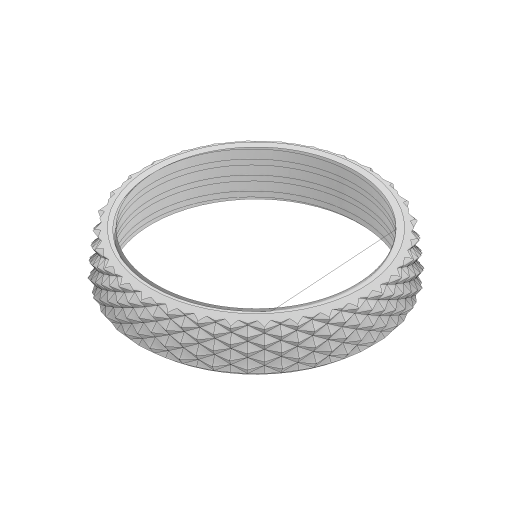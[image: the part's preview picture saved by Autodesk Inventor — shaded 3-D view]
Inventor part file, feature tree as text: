
AUTODESK INVENTOR PART (.ipt)
format: ipt  version: 2023 (Build 270158000, 158)  size: 4,238,336 bytes
history: native  units: mm
features: sketch x5, helix x3, draft x2, extrude x1, pattern_circular x1, mirror x1, revolve x1, projected_geometry x1
ambient origin geometry x8: Origin, YZ Plane, XZ Plane, XY Plane, X Axis, Y Axis, Z Axis, Center Point
bodies: Solid1 (feature_tree)
feature tree (15):
  extrude  "Extrusion1"  Depth=6.52mm TaperAngle=0.0deg
  draft  "FaceDraft1"
  sketch  "Sketch2"  dims[d7=2.0mm d8=9.0mm d9=10.0mm d10=1.047198mm d11=90.0deg d12=90.0deg d13=0.0mm d14=0.0mm d15=2.0mm d16=3.0mm d17=10.0mm d18=-1.047198mm d19=90.0deg d20=90.0deg d21=0.0mm d22=0.0mm d23=2.8mm d91=1.047198mm d109=2.094395mm]
  sketch  "Sketch4"  dims[d112=2.0mm d113=6.52mm d114=1.25mm d115=1.047198mm]
  helix  "Coil1"  [1 undecoded]
  helix  "Coil2"  [1 undecoded]
  draft  "FaceDraft2"
  helix  "Coil10"  [1 undecoded]
  pattern_circular  "Circular Pattern5"  Count=30 Angle=360.0deg
  mirror  "Mirror1"
  revolve  "Revolution2"  Angle=360.0deg
  sketch  "Sketch1"  dims[d0=26.5mm d2=6.52mm d3=0.0mm d4=1.047198mm]
  sketch  "Sketch13"  dims[d116=90.0deg d117=90.0deg d118=0.0mm d119=0.0mm d122=300.0mm d123=360.0deg]
  sketch  "Sketch14"  dims[d127=60.0deg d129=360.0deg d130=8.726646mm]
  projected_geometry  "Project Cut Edges1"
note: 3 required parameter values undecoded (feature->parameter linkage not recoverable at this tier; creation-order binding heuristic only, values carry confidence <= 0.55)
